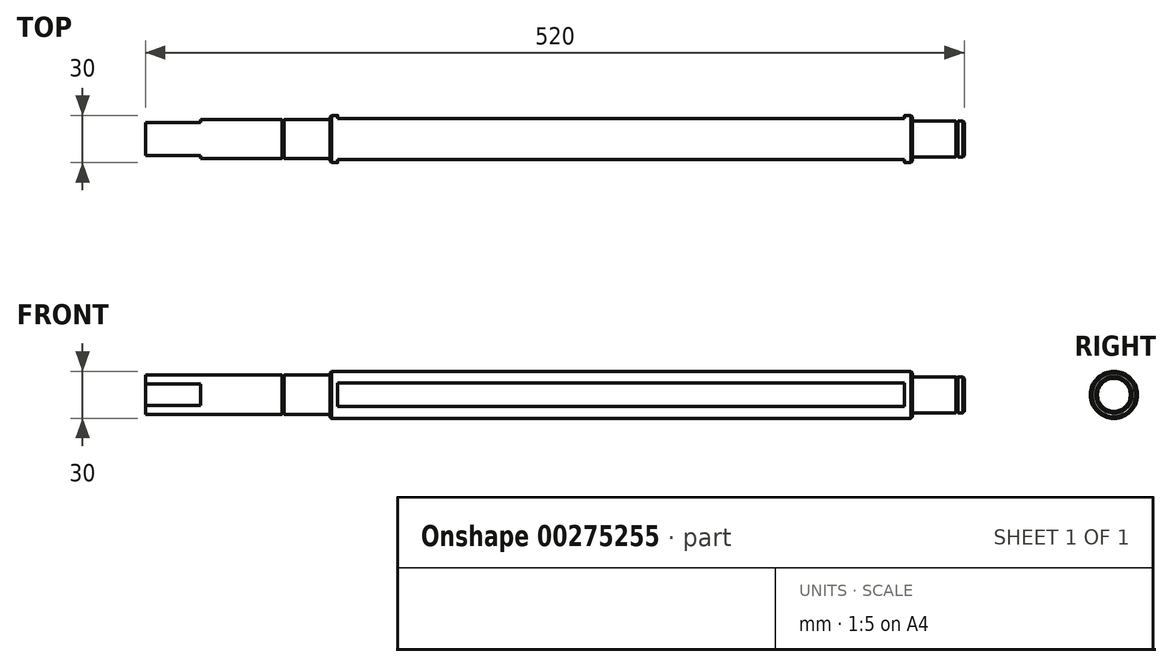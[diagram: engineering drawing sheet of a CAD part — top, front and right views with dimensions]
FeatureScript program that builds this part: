
annotation { "Feature Type Name" : "Feature", "Feature Type Description" : "" }
export const myFeature = defineFeature(function(context is Context, id is Id, definition is map)
    precondition{}
    {
        {
            var Q0;
            Q0=qCreatedBy(makeId("Front.planeOp"),FACE);
            var sketch = newSketch(context, id + "F0", { "sketchPlane" : qUnion([Q0])});
            skLineSegment(sketch, "E0", {"start": v(-302, 0) * mm, "end": v(-185, 0) * mm});
            skLineSegment(sketch, "E1", {"start": v(-185, 15) * mm, "end": v(185, 15) * mm});
            skLineSegment(sketch, "E2", {"start": v(-185, 15) * mm, "end": v(-185, 12.5) * mm});
            skLineSegment(sketch, "E3", {"start": v(-185, 12.5) * mm, "end": v(-214, 12.5) * mm});
            skLineSegment(sketch, "E4", {"start": v(-214, 12.5) * mm, "end": v(-214, 11.9) * mm});
            skLineSegment(sketch, "E5", {"start": v(-215.3, 11.9) * mm, "end": v(-215.3, 12.5) * mm});
            skLineSegment(sketch, "E6", {"start": v(-302, 12.5) * mm, "end": v(-215.3, 12.5) * mm});
            skLineSegment(sketch, "E7", {"start": v(-215.3, 11.9) * mm, "end": v(-214, 11.9) * mm});
            skLineSegment(sketch, "E8", {"start": v(-302, 12.5) * mm, "end": v(-302, 6.5) * mm});
            skLineSegment(sketch, "E9", {"start": v(185, 15) * mm, "end": v(185, 11.5) * mm});
            skLineSegment(sketch, "E10", {"start": v(218, 11.5) * mm, "end": v(218, 0) * mm});
            skLineSegment(sketch, "E11", {"start": v(185, 11.5) * mm, "end": v(212.7, 11.5) * mm});
            skLineSegment(sketch, "E12", {"start": v(214, 11.5) * mm, "end": v(214, 10.9) * mm});
            skLineSegment(sketch, "E13", {"start": v(212.7, 10.9) * mm, "end": v(214, 10.9) * mm});
            skLineSegment(sketch, "E14", {"start": v(212.7, 10.9) * mm, "end": v(212.7, 11.5) * mm});
            skLineSegment(sketch, "E15", {"start": v(214, 11.5) * mm, "end": v(218, 11.5) * mm});
            skLineSegment(sketch, "E16.trimOffspring", {"start": v(175, 0) * mm, "end": v(218, 0) * mm});
            skLineSegment(sketch, "E17", {"start": v(-185, 0) * mm, "end": v(175, 0) * mm});
            skPoint(sketch, "E18.end.orphan", {"position": v(-180, 7.5) * mm});
            skPoint(sketch, "E19.start.orphan", {"position": v(180, 7.5) * mm});
            skPoint(sketch, "E20.end.orphan", {"position": v(-272, 0) * mm});
            skLineSegment(sketch, "E21", {"start": v(-302, 6.5) * mm, "end": v(-302, 0) * mm});
            skSolve(sketch);
        }
        {
            var Q0;
            Q0=makeQuery(id+"F0.imprint","IMPRINT",FACE,{"disambiguationData":[TD([[makeQuery(id+"F0.imprint","IMPRINT",EDGE,{"derivedFrom":sQuery(id+"F0.wireOp",EDGE,"E0")}),1.0]])]});
            var Q1;
            Q1=sQuery(id+"F0.wireOp",EDGE,"E17");
            revolve(context, id + "F1", {"entities" : qUnion([Q0]), "axis" : qUnion([Q1]), "revolveType" : RevolveType.FULL});
        }
        {
            var Q0;
            Q0=qCreatedBy(makeId("Right.planeOp"),FACE);
            var sketch = newSketch(context, id + "F2", { "sketchPlane" : qUnion([Q0])});
            skArc(sketch, "E22.0", {"start": v(-13, 7.5) * mm, "mid": v(-15, 0) * mm, "end": v(-13, -7.5) * mm});
            skLineSegment(sketch, "E23", {"start": v(-13, 7.5) * mm, "end": v(-13, -7.5) * mm});
            skLineSegment(sketch, "E24", {"start": v(13, 7.5) * mm, "end": v(13, -7.5) * mm});
            skArc(sketch, "E25.trimOffspring", {"start": v(13, -7.5) * mm, "mid": v(15, 0) * mm, "end": v(13, 7.5) * mm});
            skSolve(sketch);
        }
        {
            var Q0;
            Q0 = qSketchRegion(id + "F2", true);
            extrude(context, id + "F3", {"entities" : qUnion([Q0]), "operationType" : NewBodyOperationType.REMOVE, "endBound" : BoundingType.SYMMETRIC, "oppositeDirection" : true, "depth" : 360 * mm});
        }
        {
            var Q0;
            Q0=makeQuery(id+"F1.opRevolve","SWEPT_FACE",FACE,{"disambiguationData":[OSD([sQuery(id+"F0.wireOp",EDGE,"E8"),sQuery(id+"F0.wireOp",EDGE,"E21")])]});
            var sketch = newSketch(context, id + "F4", { "sketchPlane" : qUnion([Q0])});
            skArc(sketch, "E26.0", {"start": v(-10.5, 6.78) * mm, "mid": v(-12.5, 0) * mm, "end": v(-10.5, -6.78) * mm});
            skLineSegment(sketch, "E27", {"start": v(-10.5, 6.78) * mm, "end": v(-10.5, -6.78) * mm});
            skLineSegment(sketch, "E28", {"start": v(10.5, 6.78) * mm, "end": v(10.5, -6.78) * mm});
            skLineSegment(sketch, "E29", {"start": v(0, 9.98) * mm, "end": v(0, -9.03) * mm, "construction": true});
            skArc(sketch, "E30.trimOffspring", {"start": v(10.5, -6.78) * mm, "mid": v(12.5, 0) * mm, "end": v(10.5, 6.78) * mm});
            skSolve(sketch);
        }
        {
            var Q0;
            Q0=makeQuery(id+"F4.imprint","IMPRINT",FACE,{"disambiguationData":[TD([[makeQuery(id+"F4.imprint","IMPRINT",EDGE,{"derivedFrom":sQuery(id+"F4.wireOp",EDGE,"E26.0")}),1.0]])]});
            var Q1;
            Q1=makeQuery(id+"F4.imprint","IMPRINT",FACE,{"disambiguationData":[TD([[makeQuery(id+"F4.imprint","IMPRINT",EDGE,{"derivedFrom":sQuery(id+"F4.wireOp",EDGE,"E28")}),1.0]])]});
            extrude(context, id + "F5", {"entities" : qUnion([Q0, Q1]), "operationType" : NewBodyOperationType.REMOVE, "oppositeDirection" : true, "depth" : 35 * mm});
        }
        {
            var Q0;
            Q0=makeQuery(id+"F1.opRevolve","SWEPT_EDGE",EDGE,{"disambiguationData":[OSD([sQuery(id+"F0.wireOp",EDGE,"E1"),sQuery(id+"F0.wireOp",EDGE,"E2")])]});
            var Q1;
            Q1=makeQuery(id+"F1.opRevolve","SWEPT_EDGE",EDGE,{"disambiguationData":[OSD([sQuery(id+"F0.wireOp",EDGE,"E1"),sQuery(id+"F0.wireOp",EDGE,"E9")])]});
            var Q2;
            Q2=makeQuery(id+"F1.opRevolve","SWEPT_EDGE",EDGE,{"disambiguationData":[OSD([sQuery(id+"F0.wireOp",EDGE,"E10"),sQuery(id+"F0.wireOp",EDGE,"E15")])]});
            chamfer(context, id + "F6", {"entities" : qUnion([Q0, Q1, Q2]), "width" : 1 * mm, "tangentPropagation" : true});
        }
    });
